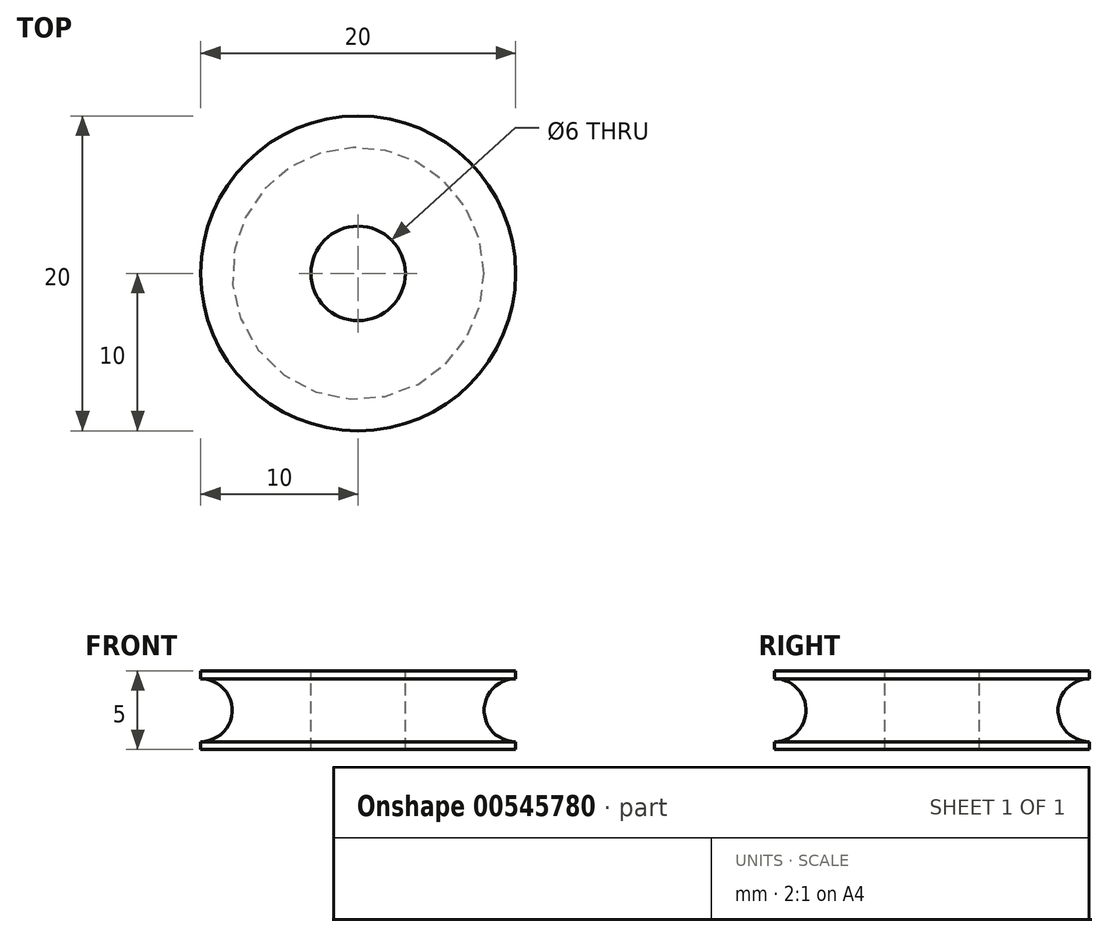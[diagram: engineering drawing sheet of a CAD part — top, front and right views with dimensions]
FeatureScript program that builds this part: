
annotation { "Feature Type Name" : "Feature", "Feature Type Description" : "" }
export const myFeature = defineFeature(function(context is Context, id is Id, definition is map)
    precondition{}
    {
        {
            var Q0;
            Q0=qCreatedBy(makeId("Top.planeOp"),FACE);
            var sketch = newSketch(context, id + "F0", { "sketchPlane" : qUnion([Q0])});
            skCircle(sketch, "E0", {"center": v(0, 0) * mm, "radius": 10 * mm});
            skSolve(sketch);
        }
        {
            var Q0;
            Q0=makeQuery(id+"F0.imprint","IMPRINT",FACE,{"disambiguationData":[TD([[makeQuery(id+"F0.imprint","IMPRINT",EDGE,{"derivedFrom":sQuery(id+"F0.wireOp",EDGE,"E0")}),1.0]])]});
            extrude(context, id + "F1", {"entities" : qUnion([Q0]), "endBound" : BoundingType.SYMMETRIC, "depth" : 5 * mm, "offsetDistance" : 25 * mm});
        }
        {
            var Q0;
            Q0=qCreatedBy(makeId("Right.planeOp"),FACE);
            var sketch = newSketch(context, id + "F2", { "sketchPlane" : qUnion([Q0])});
            skLineSegment(sketch, "E1", {"start": v(0, 0) * mm, "end": v(8, 0) * mm, "construction": true});
            skLineSegment(sketch, "E2", {"start": v(8, 0) * mm, "end": v(10, 0) * mm, "construction": true});
            skCircle(sketch, "E3", {"center": v(10, 0) * mm, "radius": 2 * mm});
            skLineSegment(sketch, "E4", {"start": v(0, 0) * mm, "end": v(0, 8.77) * mm, "construction": true});
            skSolve(sketch);
        }
        {
            var Q0;
            Q0=makeQuery(id+"F2.imprint","IMPRINT",FACE,{"disambiguationData":[TD([[makeQuery(id+"F2.imprint","IMPRINT",EDGE,{"derivedFrom":sQuery(id+"F2.wireOp",EDGE,"E3")}),1.0]])]});
            var Q1;
            Q1=sQuery(id+"F2.wireOp",EDGE,"E4");
            var Q2;
            Q2=sQuery(id+"F2.wireOp",EDGE,"E3");
            var Q3;
            Q3=sQuery(id+"F2.wireOp",EDGE,"E4");
            revolve(context, id + "F3", {"operationType" : NewBodyOperationType.REMOVE, "entities" : qUnion([Q0]), "surfaceEntities" : qUnion([Q1, Q2]), "axis" : qUnion([Q3]), "revolveType" : RevolveType.FULL, "oppositeDirection" : true});
        }
        {
            var Q0;
            Q0=makeQuery(id+"F1.opExtrude","CAP_FACE",FACE,{"disambiguationData":[OSD([sQuery(id+"F0.wireOp",EDGE,"E0")])],"isStart":false});
            var sketch = newSketch(context, id + "F4", { "sketchPlane" : qUnion([Q0])});
            skCircle(sketch, "E5", {"center": v(0, 0) * mm, "radius": 3 * mm});
            skSolve(sketch);
        }
        {
            var Q0;
            Q0=makeQuery(id+"F4.imprint","IMPRINT",FACE,{"disambiguationData":[TD([[makeQuery(id+"F4.imprint","IMPRINT",EDGE,{"derivedFrom":sQuery(id+"F4.wireOp",EDGE,"E5")}),1.0]])]});
            extrude(context, id + "F5", {"entities" : qUnion([Q0]), "operationType" : NewBodyOperationType.REMOVE, "oppositeDirection" : true, "depth" : 25 * mm, "offsetDistance" : 25 * mm});
        }
    });
